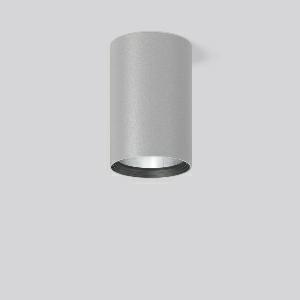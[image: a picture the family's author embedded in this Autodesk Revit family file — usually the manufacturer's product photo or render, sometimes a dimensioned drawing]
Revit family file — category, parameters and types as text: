
# Revit family: heledon_maxi_a_931216_004_76_efda
name_source: partatom
category: Lighting Fixtures
units: mm (PartAtom-declared; Revit-internal decimal feet)

## family parameters
Cut with Voids When Loaded = No
Host = Face
Light Source = No
Part Type = Normal
Room Calculation Point = No
Round Connector Dimension = Use Diameter
Shared = No

## types (1)
- HELEDON maxi A (1 x LED Modul 930, 3250 lm, 3000)
    Apparent Load = 25 VA
    Approval mark = CE
    CIE Flux Codes = 100 100 100 100 100
    Color Rendering = 90
    Color Temperature = 3000
    Default Elevation = 1800 mm
    Description = Series: HELEDON maxi
Cylindrical surface-mounted downlight. Housing: die-cast aluminium, powder-coated. Internal ceiling frame polycarbonate with bayonet mounting. Black plastic ring and recessed LED to prevent glare from the side. Optical assembly with reflector made of MIRO-Silver with 98% total light reflection for outstanding efficiency - can be changed without tools. Best colour rendering index Ra>90. Suitable for Ceiling mounting. Easy installation with a separate ceiling frame with bayonet mounting and plug connection. Driver integrated. Connected via plug-in connector. High quality converter without flickering and stroboscopic effect. The following accessories can be mounted without use of tools: interchangeable lenses, decorative glasses, honeycomb louvre, clear and frosted diffusers, white interchangeable plastic ring. 
Colour: silver
Diameter: 123 mm
Height: 183 mm
Lamp: LED
Socket: without socket
Colour temperature: 3000K
Colour rendering index (CRI): 92
System power: 25 W
Rated luminous flux: 3250 lm
Luminous efficiency: 130 lm/W
Control gear: Converter, dimmable, DALI
Protection class: I
Type of protection: IP 20
    Height = 183 mm
    Lamp = 1 x LED Modul 930
    Lamp Light Flux = 3250 lm
    Lamp count = 1
    Length = 123 mm
    Lifetime = 50000 h
    Luminous efficacy = 130 lm/W
    Manufacturer = RZB
    ModVariant = No
    Model = 931216.004.76
    Mounting Place = Ceiling
    Mounting Type = Surface mounted
    Number of Poles = 1
    OnlyDefault = Yes
    Power Factor = 1
    Product Name = HELEDON maxi A
    Product group = Surface mounted downlights
    ProductGroupID = 302
    Protection Class = Protection class I
    Protection Degree = IP 20
    RLX_Detail_Level = 1
    RLX_Emergency_Light_Flux = 0 lm
    RLX_Emergency_Type = 0
    RLX_Emergency_Type_DB = No
    RlxData = <blob elided: 98957 chars, md5=6610cdb5>
    Socket = socket
    Standby Power = 0 W
    System Light Flux = 3250 lm
    System Power = 25 W
    Type Comments = Product without accessories
    Type Image = 931192.004.jpg
    URL = http://relux.com
    VarID = ---
    Voltage = 230 V
    Voltage Range = 220-240 V
    Weight = 0.00 kg
    Width = 0 mm  [stored 0 ft]

note: [stored X ft] marks values corroborated as IEEE doubles in the binary element streams (Revit-internal decimal feet)

## geometry (parser evidence)
native form markers: Blend x4, Sweep x9
no freeform markers — native parametric forms only
